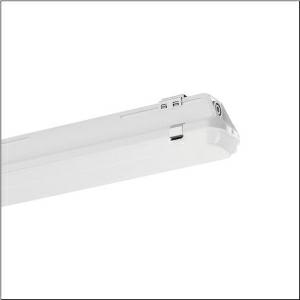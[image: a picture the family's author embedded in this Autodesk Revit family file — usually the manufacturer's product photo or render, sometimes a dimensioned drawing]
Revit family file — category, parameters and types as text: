
# Revit family: monsun_r__12_51fp10mp680h_b3aa
name_source: partatom
category: Lighting Fixtures
units: mm (PartAtom-declared; Revit-internal decimal feet)

## family parameters
Cut with Voids When Loaded = No
Host = Face
Light Source = No
Part Type = Normal
Room Calculation Point = No
Round Connector Dimension = Use Diameter
Shared = No

## types (1)
- --- (1 x LED, 7970 lm, 45.4 W, 6500K)
    Apparent Load = 45 VA
    CIE Flux Codes = 47 77 93 94 100
    Color Rendering = 80
    Color Temperature = 6500K
    Default Elevation = 1800 mm
    Description = Monsun® 12, damp-proof luminaire, chain hanger, primary optical cover: enclosure, of PMMA, light emission: direct distribution, primary light characteristic: symmetric, installation type: suspended mounting, surface-mounted, horizontal mounting, vertical mounting, LED rated luminous flux: 7.970 lm, light colour: 865, colour temperature: 6500K, control gear: ECG, with terminal, 3-pole, max. 2.5mm², mains connection: 220..240V, AC, 50/60Hz, rated input power: 45W, luminaire housing, of glass-fibre reinforced polyester, uncoated, bright grey, length: 1.590 mm, width: 90 mm, height: 88mm, clip for enclosure, of stainless steel (V2A), ceiling mounting element, of stainless steel (V2A), chain hanger, of stainless steel (V2A), protection rating (complete): IP66, insulation class (complete): insulation class I (protective earthing), certification: CE, ENEC, VDE, protection symbol: D, impact resistance: IK04, permissible ambient temperature for indoor applications: -35..+40°C, standard: EN 50419, EN 60598-2-1, no direct snow, no direct sun, no direct rain, for indoor or canopied outdoor use, corresponds to IFS (International Featured Standards) requirements for safety and quality in the food industry, for animal farming (ammonia tested): for use in cowhouse, pig house, horse-stables... (not for use in poultry stables), AT max for animal farming = 40°C, packaging unit: 1 piece
    Height = 89 mm
    Lamp = 1 x LED
    Lamp Light Flux = 7970 lm
    Lamp Power = 45.4 W
    Lamp count = 1
    Length = 1590 mm
    Luminous efficacy = 176 lm/W
    Manufacturer = Siteco
    ModVariant = No
    Model = 51FP10MP680H
    Mounting Place = Ceiling
    Mounting Type = Pendant
    Number of Poles = 1
    OnlyDefault = Yes
    Power Factor = 1
    Product Name = Monsun® 12
    Product group = damp-proof luminaire | ceiling pendant
    ProductGroupID = 908
    Protection Class = Protection class I
    Protection Degree = IP 66
    RLX_Detail_Level = 1
    RlxData = <blob elided: 89781 chars, md5=d878a85d>
    Socket = socket
    Standby Power = 0 W
    System Light Flux = 7970 lm
    System Power = 45 W
    Type Comments = factory setting: luminous flux: 100 % | (A | C | E) | 105 mA
    Type Image = l_1004748.jpg
    URL = http://relux.com
    VarID = @adj_136465
    Voltage = 0 V
    Weight = 0.00 kg
    Width = 90 mm

## geometry (parser evidence)
native form markers: Blend x4, Sweep x14
no freeform markers — native parametric forms only
